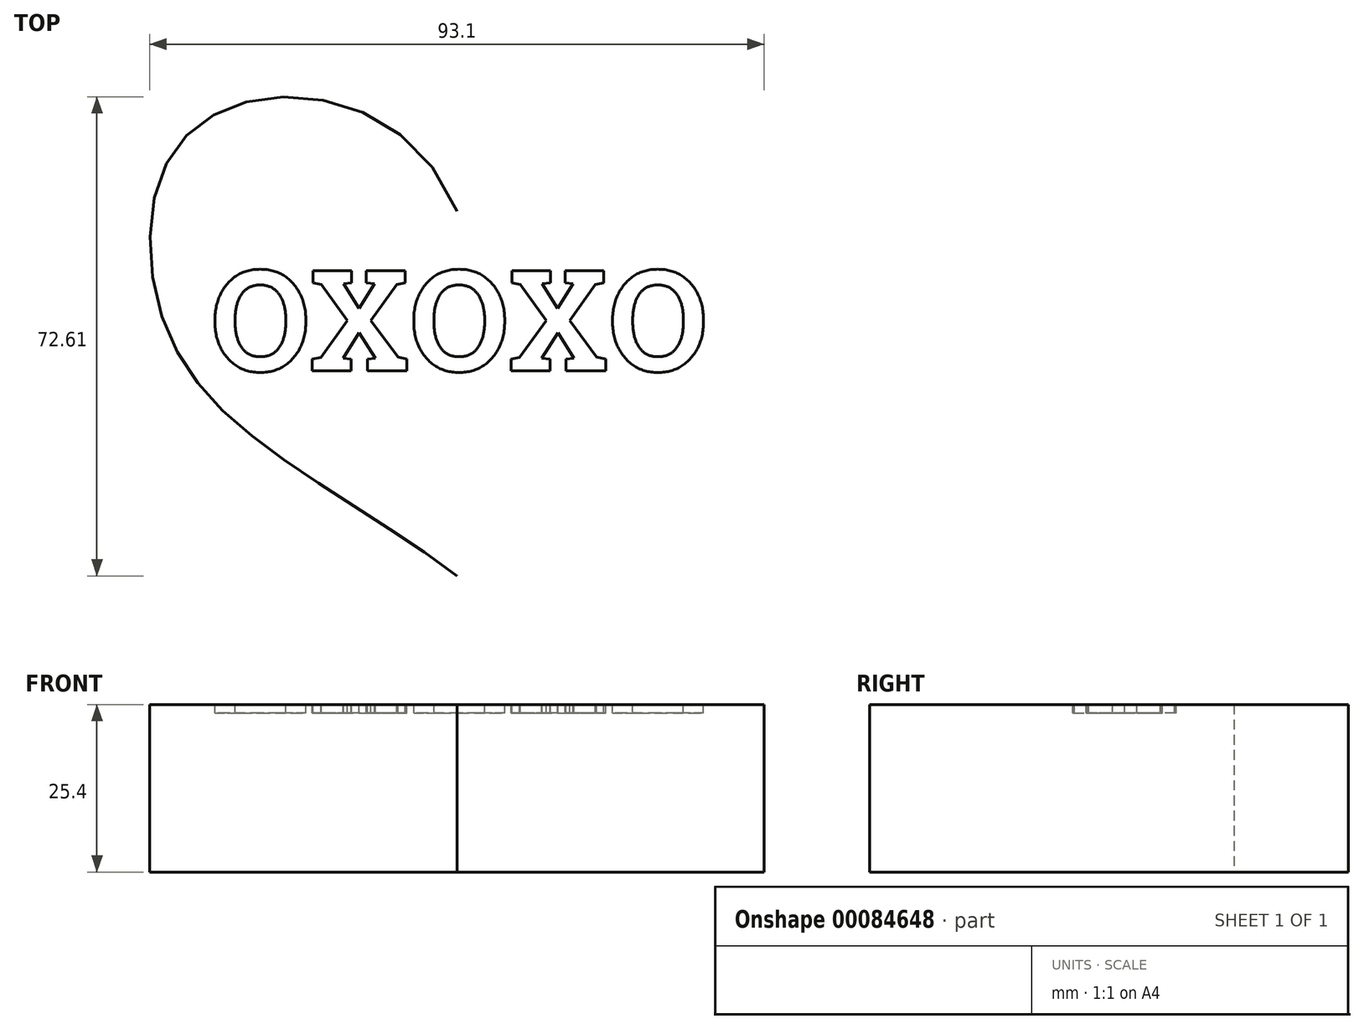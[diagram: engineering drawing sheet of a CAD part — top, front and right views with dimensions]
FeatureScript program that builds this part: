
annotation { "Feature Type Name" : "Feature", "Feature Type Description" : "" }
export const myFeature = defineFeature(function(context is Context, id is Id, definition is map)
    precondition{}
    {
        {
            var Q0;
            Q0=qCreatedBy(makeId("Top.planeOp"),FACE);
            var sketch = newSketch(context, id + "F0", { "sketchPlane" : qUnion([Q0])});
            skFitSpline(sketch, "E0", {"points": [v(0, 0) * mm, v(-26.11, 17.35) * mm, v(-44, 7.33) * mm, v(-43.64, -18.78) * mm, v(-26.11, -37.74) * mm, v(0, -55.26) * mm], "startDerivative": vector(-68.9, 174.73) * mm, "endDerivative": vector(107.51, -83.08) * mm});
            skLineSegment(sketch, "E1", {"start": v(0, 0) * mm, "end": v(0, -55.26) * mm});
            skSolve(sketch);
        }
        {
            var Q0;
            Q0 = qSketchRegion(id + "F0", true);
            var Q1;
            Q1=makeQuery(id+"F0.imprint","IMPRINT",FACE,{"disambiguationData":[TD([[makeQuery(id+"F0.imprint","IMPRINT",EDGE,{"derivedFrom":sQuery(id+"F0.wireOp",EDGE,"E0")}),1.0]])]});
            extrude(context, id + "F1", {"entities" : qUnion([Q0, Q1]), "depth" : 25.4 * mm});
        }
        {
            var Q0;
            Q0=makeQuery(id+"F1.opExtrude","SWEPT_BODY",BODY,{"disambiguationData":[OSD([sQuery(id+"F0.wireOp",EDGE,"E0"),sQuery(id+"F0.wireOp",EDGE,"E1")])]});
            var Q1;
            Q1=qCreatedBy(makeId("Right.planeOp"),FACE);
            mirror(context, id + "F2", {"operationType" : NewBodyOperationType.ADD, "entities" : qUnion([Q0]), "mirrorPlane" : qUnion([Q1])});
        }
        {
            var Q0;
            {var subQ0=makeQuery(id+"F1.opExtrude","CAP_FACE",FACE,{"disambiguationData":[OSD([sQuery(id+"F0.wireOp",EDGE,"E0"),sQuery(id+"F0.wireOp",EDGE,"E1")])],"isStart":false});Q0=makeQuery(id+"F2.boolean.opBoolean","MERGE",FACE,{"derivedFrom":[subQ0,makeQuery(id+"F2.opPattern","COPY",FACE,{"derivedFrom":subQ0,"instanceName":"1"})]});}
            var sketch = newSketch(context, id + "F3", { "sketchPlane" : qUnion([Q0])});
            skText(sketch, "E2", { "text": "OXOXO\n", "fontName": "RobotoSlab-Bold.ttf"});
            const initialGuessF3  = {"E2": [-0.03738, -0.0242, 1, 0, 0.0154]};
            skSetInitialGuess(sketch, initialGuessF3);
            skSolve(sketch);
        }
        {
            var Q0;
            Q0=makeQuery(id+"F3.imprint","IMPRINT",FACE,{"disambiguationData":[TD([[makeQuery(id+"F3.imprint","IMPRINT",EDGE,{"derivedFrom":sQuery(id+"F3.wireOp",EDGE,"E2.sketch_text.stroke-20")}),-1.0]])]});
            var Q1;
            Q1=makeQuery(id+"F3.imprint","IMPRINT",FACE,{"disambiguationData":[TD([[makeQuery(id+"F3.imprint","IMPRINT",EDGE,{"derivedFrom":sQuery(id+"F3.wireOp",EDGE,"E2.sketch_text.stroke-68")}),-1.0]])]});
            var Q2;
            Q2=makeQuery(id+"F3.imprint","IMPRINT",FACE,{"disambiguationData":[TD([[makeQuery(id+"F3.imprint","IMPRINT",EDGE,{"derivedFrom":sQuery(id+"F3.wireOp",EDGE,"E2.sketch_text.stroke-0")}),-1.0]])]});
            var Q3;
            Q3=makeQuery(id+"F3.imprint","IMPRINT",FACE,{"disambiguationData":[TD([[makeQuery(id+"F3.imprint","IMPRINT",EDGE,{"derivedFrom":sQuery(id+"F3.wireOp",EDGE,"E2.sketch_text.stroke-48")}),-1.0]])]});
            var Q4;
            Q4=makeQuery(id+"F3.imprint","IMPRINT",FACE,{"disambiguationData":[TD([[makeQuery(id+"F3.imprint","IMPRINT",EDGE,{"derivedFrom":sQuery(id+"F3.wireOp",EDGE,"E2.sketch_text.stroke-96")}),-1.0]])]});
            extrude(context, id + "F4", {"entities" : qUnion([Q0, Q1, Q2, Q3, Q4]), "operationType" : NewBodyOperationType.REMOVE, "oppositeDirection" : true, "depth" : 1.27 * mm});
        }
    });
